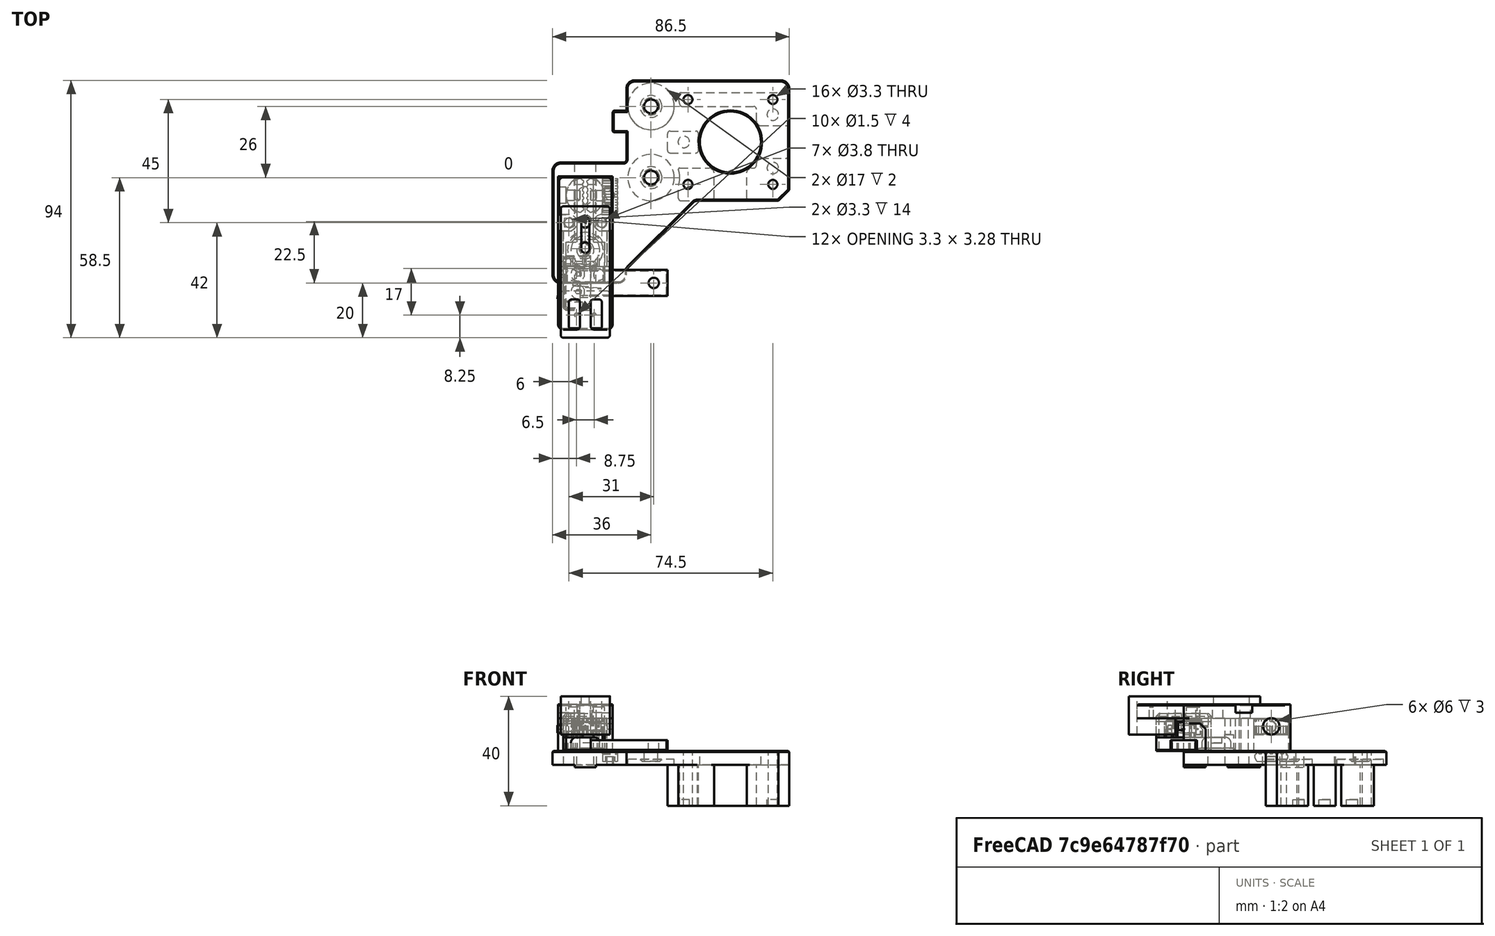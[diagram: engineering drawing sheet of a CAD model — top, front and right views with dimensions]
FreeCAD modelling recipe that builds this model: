
FCSTD DOCUMENT  (FreeCAD 0.19R24291 (Git))
Label: endstop
License: Other
LicenseURL: GPL3
objects: Part::Cylinder×31, Part::Box×27, Part::Cut×25, Part::Feature×20, Part::MultiFuse×18, Part::Chamfer×12, Part::Fillet×7, App::Part×3, Part::MultiCommon×1
note: 141 computed .brp shape members not serialized (recipe doc carries the construction recipe); baked Part::Feature solids carry a one-line shape summary decoded from their .brp

FEATURE [Part::Feature] Cut002008023012009006003002001  label="Cut002008023012009006003003"
  Placement = pos=(15,44,-35) rot=(0,0,1;0rad)
  shape: bbox 86.5 x 74 x 20 mm, 140 faces (baked)
FEATURE [Part::Feature] Fusion001001001001  label="switch"
  Placement = pos=(0,0,6) rot=(0,0,1;0rad)
  shape: bbox 13 x 12.18 x 6 mm, 43 faces (baked)
FEATURE [Part::Cylinder] Cylinder
  Angle = 360
  AttacherType = Attacher::AttachEngine3D
  Height = 1
  Placement = pos=(0,12,0) rot=(0,0,1;0rad)
  Radius = 6.5
FEATURE [Part::Cylinder] Cylinder001
  Angle = 360
  AttacherType = Attacher::AttachEngine3D
  Height = 4
  Placement = pos=(0,12,3) rot=(0,0,1;0rad)
  Radius = 2
FEATURE [Part::Cylinder] Cylinder002
  Angle = 360
  AttacherType = Attacher::AttachEngine3D
  Height = 4
  Placement = pos=(0,12,1) rot=(0,0,1;0rad)
  Radius = 5.25
FEATURE [Part::Fillet] Fillet
  Base = -> Cylinder002
  Edges = 1 edges r=2: [Edge1]
FEATURE [Part::Cut] Cut
  Base = -> Fillet
  Tool = -> Cylinder001
FEATURE [Part::Cylinder] Cylinder003
  Angle = 360
  AttacherType = Attacher::AttachEngine3D
  Height = 4
  Placement = pos=(-3.25,5.25,4) rot=(0,0,1;0rad)
  Radius = 0.75
FEATURE [Part::Cylinder] Cylinder004
  Angle = 360
  AttacherType = Attacher::AttachEngine3D
  Height = 4
  Placement = pos=(3.25,5.25,4) rot=(0,0,1;0rad)
  Radius = 0.75
FEATURE [Part::Box] Box  label="Cube"
  AttacherType = Attacher::AttachEngine3D
  Height = 5
  Length = 20
  Placement = pos=(-10,0,12) rot=(0,0,1;0rad)
  Width = 15
FEATURE [Part::Cylinder] Cylinder005
  Angle = 360
  AttacherType = Attacher::AttachEngine3D
  Height = 3
  Placement = pos=(6,22,0) rot=(0,0,1;0rad)
  Radius = 3
FEATURE [Part::Cylinder] Cylinder006
  Angle = 360
  AttacherType = Attacher::AttachEngine3D
  Height = 3
  Placement = pos=(-6,22,0) rot=(0,0,1;0rad)
  Radius = 3
FEATURE [Part::Box] Box001  label="Cube001"
  AttacherType = Attacher::AttachEngine3D
  Height = 17
  Length = 20
  Placement = pos=(-10,15,0) rot=(0,0,1;0rad)
  Width = 24
FEATURE [Part::Box] Box003  label="Cube003"
  AttacherType = Attacher::AttachEngine3D
  Height = 17
  Length = 3
  Placement = pos=(-10,0,0) rot=(0,0,1;0rad)
  Width = 39
FEATURE [Part::Cylinder] Cylinder007
  Angle = 360
  AttacherType = Attacher::AttachEngine3D
  Height = 6
  Placement = pos=(0,32,0) rot=(0,0,1;0rad)
  Radius = 7
FEATURE [Part::Cylinder] Cylinder008
  Angle = 360
  AttacherType = Attacher::AttachEngine3D
  Height = 6
  Placement = pos=(0,12,0) rot=(0,0,1;0rad)
  Radius = 7
FEATURE [Part::MultiFuse] Fusion
  Shapes = -> [Cylinder008,Cylinder007]
FEATURE [Part::Cylinder] Cylinder009
  Angle = 360
  AttacherType = Attacher::AttachEngine3D
  Height = 42
  Placement = pos=(6,22,0) rot=(0,0,1;0rad)
  Radius = 1.65
FEATURE [Part::Cylinder] Cylinder010
  Angle = 360
  AttacherType = Attacher::AttachEngine3D
  Height = 42
  Placement = pos=(-6,22,0) rot=(0,0,1;0rad)
  Radius = 1.65
FEATURE [Part::MultiFuse] Fusion001001001003
  Shapes = -> [Cylinder009,Cylinder010]
FEATURE [Part::MultiFuse] Fusion001001001004
  Placement = pos=(0,0,14) rot=(0,0,1;0rad)
  Shapes = -> [Cylinder006,Cylinder005]
FEATURE [Part::Box] Box004  label="Cube004"
  AttacherType = Attacher::AttachEngine3D
  Height = 10
  Length = 10
  Placement = pos=(6,19,14) rot=(0,0,1;0rad)
  Width = 6
FEATURE [Part::Box] Box005  label="Cube005"
  AttacherType = Attacher::AttachEngine3D
  Height = 10
  Length = 10
  Placement = pos=(-16,19,14) rot=(0,0,1;0rad)
  Width = 6
FEATURE [Part::MultiFuse] Fusion001001001005
  Shapes = -> [Box005,Box004]
FEATURE [Part::Box] Box006  label="Cube006"
  AttacherType = Attacher::AttachEngine3D
  Height = 12
  Length = 6
  Placement = pos=(-3,13,0) rot=(0,0,1;0rad)
  Width = 32
FEATURE [Part::MultiFuse] Fusion001001001006
  Placement = pos=(0,0,8) rot=(0,0,1;0rad)
  Shapes = -> [Cylinder004,Cylinder003]
FEATURE [Part::Box] Box007  label="Cube007"
  AttacherType = Attacher::AttachEngine3D
  Height = 17
  Length = 3
  Placement = pos=(7,0,0) rot=(0,0,1;0rad)
  Width = 39
FEATURE [Part::MultiFuse] Fusion001001001008
  Shapes = -> [Box007,Box001,Box,Box003]
FEATURE [Part::Cut] Cut002008023012009006003002002
  Base = -> Fusion001001001008
  Tool = -> Fusion
FEATURE [Part::Cut] Cut002008023012009006003002003
  Base = -> Cut002008023012009006003002002
  Tool = -> Box006
FEATURE [Part::Cut] Cut002008023012009006003002004
  Base = -> Cut002008023012009006003002003
  Tool = -> Fusion001001001003
FEATURE [Part::Cut] Cut002008023012009006003002005
  Base = -> Cut002008023012009006003002004
  Tool = -> Fusion001001001005
FEATURE [Part::Cut] Cut002008023012009006003002006  label="base-endstop-mount-template"
  Base = -> Cut002008023012009006003002005
  Tool = -> Fusion001001001004
FEATURE [Part::Feature] Cut002008023012009006003002006001  label="base-endstop-mount-template001"
  shape: bbox 20 x 39 x 17 mm, 32 faces (baked)
FEATURE [Part::Fillet] Fillet001
  Base = -> Cut002008023012009006003002006001
  Edges = 4 edges r=2: [Edge26,Edge28,Edge77,Edge104]
FEATURE [Part::Chamfer] Chamfer
  Base = -> Fillet001
  Edges = 2 edges r=2: [Edge93,Edge110]
FEATURE [Part::Chamfer] Chamfer001
  Base = -> Chamfer
  Edges = 10 edges r=0.4: [Edge30,Edge39,Edge70,Edge71,Edge74,Edge76,Edge77,Edge79,Edge82,Edge84]
FEATURE [Part::Feature] Cut002008023012009006003002006002002  label="base-endstop-mount-template002"
  shape: bbox 20 x 39 x 17 mm, 32 faces (baked)
FEATURE [Part::Box] Box008  label="Cube008"
  AttacherType = Attacher::AttachEngine3D
  Height = 12
  Length = 16
  Placement = pos=(-8,0,-2) rot=(0,0,1;0rad)
  Width = 19
FEATURE [Part::Fillet] Fillet002
  Base = -> Cut002008023012009006003002006002002
  Edges = 4 edges r=2: [Edge26,Edge28,Edge77,Edge104]
FEATURE [Part::Chamfer] Chamfer002
  Base = -> Fillet002
  Edges = 10 edges r=0.4: [Edge1,Edge9,Edge10,Edge13,Edge15,Edge16,Edge18,Edge20,Edge22,Edge24]
FEATURE [Part::Cylinder] Cylinder011
  Angle = 360
  AttacherType = Attacher::AttachEngine3D
  Height = 10
  Placement = pos=(5,3,6) rot=(0,0,1;0rad)
  Radius = 2
FEATURE [Part::Cylinder] Cylinder012
  Angle = 360
  AttacherType = Attacher::AttachEngine3D
  Height = 10
  Placement = pos=(-5,3,6) rot=(0,0,1;0rad)
  Radius = 2
FEATURE [Part::MultiFuse] Fusion001001001009
  Shapes = -> [Cylinder012,Cylinder011]
FEATURE [Part::Box] Box009  label="Cube009"
  AttacherType = Attacher::AttachEngine3D
  Height = 12
  Length = 22
  Placement = pos=(-11,-12,-2) rot=(0,0,1;0rad)
  Width = 19
FEATURE [Part::Box] Box010  label="Cube010"
  AttacherType = Attacher::AttachEngine3D
  Height = 3
  Length = 16
  Placement = pos=(-8,0,10) rot=(0,0,1;0rad)
  Width = 6
FEATURE [Part::Cut] Cut002008023012009006003002006002003
  Base = -> Chamfer002
  Tool = -> Box008
FEATURE [Part::Box] Box011  label="Cube011"
  AttacherType = Attacher::AttachEngine3D
  Height = 3
  Length = 16
  Placement = pos=(-8,0,9) rot=(0,0,1;0rad)
  Width = 19
FEATURE [Part::Cut] Cut002008023012009006003002006002004
  Base = -> Cut002008023012009006003002006002003
  Tool = -> Box011
FEATURE [Part::MultiFuse] Fusion001001001010
  Shapes = -> [Cut002008023012009006003002006002004,Box010]
FEATURE [Part::Cut] Cut002008023012009006003002006002005
  Base = -> Fusion001001001010
  Tool = -> Fusion001001001009
FEATURE [Part::Chamfer] Chamfer003
  Base = -> Cut002008023012009006003002006002005
  Edges = 2 edges r=2: [Edge106,Edge148]
FEATURE [Part::Chamfer] Chamfer004
  Base = -> Box009
  Edges = 1 edges r=2: [Edge12]
  Placement = pos=(0,1,0) rot=(0,0,1;0rad)
FEATURE [Part::Cut] Cut002008023012009006003002006002006  label="HTU2X-sensor-mounter"
  Base = -> Chamfer003
  Tool = -> Chamfer004
FEATURE [Part::Cut] Cut002008023012009006003002006002006002
  Base = -> Chamfer001
  Tool = -> Fusion001001001006
FEATURE [Part::Cylinder] Cylinder013
  Angle = 360
  AttacherType = Attacher::AttachEngine3D
  Height = 5.5
  Placement = pos=(0,32,6.25) rot=(0,0,1;0rad)
  Radius = 6.5
FEATURE [Part::Box] Box012  label="Cube012"
  AttacherType = Attacher::AttachEngine3D
  Height = 10
  Length = 10
  Placement = pos=(-9,20.75,2.25) rot=(0,0,1;0rad)
  Width = 19
FEATURE [Part::Cylinder] Cylinder014
  Angle = 360
  AttacherType = Attacher::AttachEngine3D
  Height = 12
  Placement = pos=(0,32,0) rot=(0,0,1;0rad)
  Radius = 7
FEATURE [Part::Box] Box013  label="Cube013"
  AttacherType = Attacher::AttachEngine3D
  Height = 16
  Length = 10
  Placement = pos=(4,20.75,-2.25) rot=(0,0,1;0rad)
  Width = 19
FEATURE [Part::Box] Box014  label="Cube014"
  AttacherType = Attacher::AttachEngine3D
  Height = 16
  Length = 10
  Placement = pos=(-10,20.75,-2.25) rot=(0,0,1;0rad)
  Width = 19
FEATURE [Part::Cut] Cut002008023012009006003002006002006002003
  Base = -> Cylinder014
  Tool = -> Box014
FEATURE [Part::Cut] Cut002008023012009006003002006002006002004
  Base = -> Cut002008023012009006003002006002006002003
  Tool = -> Box013
FEATURE [Part::Feature] Cut002008023012009006003002006002006002004001  label="Cut002008023012009006003002006002006002005"
  shape: bbox 4 x 14 x 12 mm, 6 faces (baked)
FEATURE [Part::Cut] Cut002008023012009006003002006002006002004002
  Base = -> Cut002008023012009006003002006002006002
  Tool = -> Cut002008023012009006003002006002006002004001
FEATURE [Part::Cut] Cut002008023012009006003002006002006002004003
  Base = -> Cut002008023012009006003002006002006
  Tool = -> Cut002008023012009006003002006002006002004
FEATURE [Part::Cylinder] Cylinder015
  Angle = 360
  AttacherType = Attacher::AttachEngine3D
  Height = 3
  Placement = pos=(7,32,9) rot=(0,1,0;1.5708rad)
  Radius = 3
FEATURE [Part::Cylinder] Cylinder016
  Angle = 360
  AttacherType = Attacher::AttachEngine3D
  Height = 16
  Placement = pos=(-2e-15,32,9) rot=(0,1,0;1.5708rad)
  Radius = 1.9
FEATURE [Part::MultiFuse] Fusion001001001011
  Shapes = -> [Cylinder016,Cylinder015]
FEATURE [Part::Feature] Fusion001001001011001  label="Fusion001001001012"
  shape: bbox 16 x 6 x 6 mm, 7 faces (baked)
FEATURE [Part::Cut] Cut002008023012009006003002006002006002004004  label="endstop-mount"
  Base = -> Cut002008023012009006003002006002006002004002
  Tool = -> Fusion001001001011001
FEATURE [Part::Cut] Cut002008023012009006003002006002006002004005  label="sensor-mount"
  Base = -> Cut002008023012009006003002006002006002004003
  Tool = -> Fusion001001001011
FEATURE [Part::Box] Box015  label="Cube015"
  AttacherType = Attacher::AttachEngine3D
  Height = 10
  Length = 10
  Placement = pos=(3.75,20.75,2.25) rot=(0,0,1;0rad)
  Width = 19
FEATURE [Part::Cut] Cut002008023012009006003002006002006002004006
  Base = -> Cylinder013
  Tool = -> Box015
FEATURE [Part::Cut] Cut002008023012009006003002006002006002004007
  Base = -> Cut002008023012009006003002006002006002004006
  Tool = -> Box012
FEATURE [Part::Fillet] Fillet003
  Base = -> Cut002008023012009006003002006002006002004007
  Edges = 2 edges r=1: [Edge2,Edge8]
FEATURE [Part::Cylinder] Cylinder017
  Angle = 360
  AttacherType = Attacher::AttachEngine3D
  Height = 10
  Placement = pos=(2,32,9) rot=(0,1,0;1.5708rad)
  Radius = 1.7
FEATURE [Part::Cut] Cut002008023012009006003002006002006002004008
  Base = -> Fillet003
  Tool = -> Cylinder017
FEATURE [Part::Cylinder] Cylinder018
  Angle = 360
  AttacherType = Attacher::AttachEngine3D
  Height = 5.5
  Placement = pos=(1,27,6.25) rot=(0,0,1;0rad)
  Radius = 0.5
FEATURE [Part::Cylinder] Cylinder020
  Angle = 360
  AttacherType = Attacher::AttachEngine3D
  Height = 5.5
  Placement = pos=(1,35,6.25) rot=(0,0,1;0rad)
  Radius = 0.5
FEATURE [Part::Cylinder] Cylinder021
  Angle = 360
  AttacherType = Attacher::AttachEngine3D
  Height = 5.5
  Placement = pos=(1,37,6.25) rot=(0,0,1;0rad)
  Radius = 0.5
FEATURE [Part::Cylinder] Cylinder022
  Angle = 360
  AttacherType = Attacher::AttachEngine3D
  Height = 5.5
  Placement = pos=(1,31,6.25) rot=(0,0,1;0rad)
  Radius = 0.5
FEATURE [Part::Cylinder] Cylinder023
  Angle = 360
  AttacherType = Attacher::AttachEngine3D
  Height = 5.5
  Placement = pos=(1,29,6.25) rot=(0,0,1;0rad)
  Radius = 0.5
FEATURE [Part::Cylinder] Cylinder024
  Angle = 360
  AttacherType = Attacher::AttachEngine3D
  Height = 5.5
  Placement = pos=(1,33,6.25) rot=(0,0,1;0rad)
  Radius = 0.5
FEATURE [Part::MultiFuse] Fusion001001001011002  label="wire-clamp"
  Shapes = -> [Cylinder024,Cylinder022,Cylinder020,Cylinder021,Cylinder023,Cylinder018,Cut002008023012009006003002006002006002004008]
FEATURE [Part::Feature] Cut002008023012009006003002006002006002004004001  label="endstop-mount001"
  shape: bbox 20 x 39 x 17 mm, 57 faces (baked)
FEATURE [Part::Feature] Fusion001001001011002001  label="wire-clamp001"
  shape: bbox 3.25 x 12.25 x 5.5 mm, 20 faces (baked)
FEATURE [Part::Feature] Part__Mirroring001001  label="wire-clamp002 (Mirror #2)001"
  shape: bbox 3.25 x 12.25 x 5.5 mm, 20 faces (baked)
FEATURE [Part::Feature] Part__Mirroring001002  label="sensor-mount001 (Mirror #1)001"
  shape: bbox 20 x 39 x 17 mm, 59 faces (baked)
FEATURE [App::Part] Part001  label="HTU2X-mounter"
  Group = -> [Part__Mirroring001001,Part__Mirroring001002]
  Origin = -> Origin001
FEATURE [Part::Feature] Fusion001001001011002002  label="switch001"
  Placement = pos=(0,0,6) rot=(0,0,1;0rad)
  shape: bbox 13 x 12.18 x 6 mm, 43 faces (baked)
FEATURE [App::Part] Part  label="Y-endstop"
  Group = -> [Cut002008023012009006003002006002006002004004001,Fusion001001001011002001,Fusion001001001011002002]
  Origin = -> Origin
FEATURE [Part::Box] Box018  label="Cube018"
  AttacherType = Attacher::AttachEngine3D
  Height = 4
  Length = 30
  Placement = pos=(0,-4.8,0) rot=(0,0,1;0rad)
  Width = 9.6
FEATURE [Part::Feature] Fusion001001001011002003  label="switch002"
  Placement = pos=(-8,2e-15,5) rot=(0,0,-1;1.5708rad)
  shape: bbox 12.18 x 13 x 6 mm, 43 faces (baked)
FEATURE [Part::Box] Box019  label="Cube019"
  AttacherType = Attacher::AttachEngine3D
  Height = 5
  Length = 10
  Placement = pos=(-8,-10,0) rot=(0,0,1;0rad)
  Width = 20
FEATURE [Part::Box] Box020  label="Cube020"
  AttacherType = Attacher::AttachEngine3D
  Height = 7
  Length = 7
  Placement = pos=(-8,-10,5) rot=(0,0,1;0rad)
  Width = 3
FEATURE [Part::Box] Box021  label="Cube021"
  AttacherType = Attacher::AttachEngine3D
  Height = 7
  Length = 7
  Placement = pos=(-8,7,5) rot=(0,0,1;0rad)
  Width = 3
FEATURE [Part::Box] Box022  label="Cube022"
  AttacherType = Attacher::AttachEngine3D
  Height = 3
  Length = 10
  Placement = pos=(-8,-10,10.5) rot=(0,0,1;0rad)
  Width = 20
FEATURE [Part::Chamfer] Chamfer009
  Base = -> Box019
  Edges = 2 edges r=1: [Edge1,Edge3]
FEATURE [Part::Chamfer] Chamfer010
  Base = -> Box021
  Edges = 1 edges r=1: [Edge3]
FEATURE [Part::Chamfer] Chamfer011
  Base = -> Box020
  Edges = 1 edges r=1: [Edge1]
FEATURE [Part::Chamfer] Chamfer012
  Base = -> Box022
  Edges = 2 edges r=1: [Edge1,Edge3]
FEATURE [Part::Chamfer] Chamfer013
  Base = -> Chamfer012
  Edges = 5 edges r=1: [Edge1,Edge5,Edge6,Edge7,Edge8]
FEATURE [Part::Cylinder] Cylinder025
  Angle = 360
  AttacherType = Attacher::AttachEngine3D
  Height = 5
  Placement = pos=(25,0,0) rot=(0,0,1;0rad)
  Radius = 1.9
FEATURE [Part::Cut] Cut002008023012009006003002006002006002004004002
  Base = -> Box018
  Tool = -> Cylinder025
FEATURE [Part::MultiFuse] Fusion001001001011002004
  Shapes = -> [Chamfer009,Cut002008023012009006003002006002006002004004002]
FEATURE [Part::Cylinder] Cylinder026
  Angle = 360
  AttacherType = Attacher::AttachEngine3D
  Height = 5
  Placement = pos=(-2.75,3.25,0) rot=(0,0,1;0rad)
  Radius = 2.5
FEATURE [Part::Cylinder] Cylinder027
  Angle = 360
  AttacherType = Attacher::AttachEngine3D
  Height = 5
  Placement = pos=(-2.75,-3.25,0) rot=(0,0,1;0rad)
  Radius = 2.5
FEATURE [Part::Cylinder] Cylinder028
  Angle = 360
  AttacherType = Attacher::AttachEngine3D
  Height = 18
  Placement = pos=(-2.75,-3.25,0) rot=(0,0,1;0rad)
  Radius = 0.85
FEATURE [Part::Cylinder] Cylinder029
  Angle = 360
  AttacherType = Attacher::AttachEngine3D
  Height = 18
  Placement = pos=(-2.75,3.25,0) rot=(0,0,1;0rad)
  Radius = 0.85
FEATURE [Part::MultiFuse] Fusion001001001011002005
  Shapes = -> [Cylinder028,Cylinder029]
FEATURE [Part::Cut] Cut002008023012009006003002006002006002004004003
  Base = -> Chamfer013
  Placement = pos=(0,0,0.5) rot=(0,0,1;0rad)
  Tool = -> Fusion001001001011002005
FEATURE [Part::MultiFuse] Fusion001001001011002006
  Placement = pos=(0,0,12) rot=(0,0,1;0rad)
  Shapes = -> [Cylinder027,Cylinder026]
FEATURE [Part::Feature] Fusion001001001011002004001  label="Fusion001001001011002007"
  shape: bbox 38 x 20 x 5 mm, 13 faces (baked)
FEATURE [Part::Chamfer] Chamfer014
  Base = -> Fusion001001001011002004001
  Edges = 12 edges r=0.4: [Edge4,Edge10,Edge12,Edge14,Edge16,Edge18,Edge22,Edge23,Edge24,Edge29,Edge30,Edge31]
FEATURE [Part::Cut] Cut002008023012009006003002006002006002004004004
  Base = -> Cut002008023012009006003002006002006002004004003
  Placement = pos=(0,0,-0.25) rot=(0,0,1;0rad)
  Tool = -> Fusion001001001011002006
FEATURE [Part::MultiFuse] Fusion001001001011002004002
  Shapes = -> [Cut002008023012009006003002006002006002004004004,Chamfer010,Chamfer011]
FEATURE [Part::Feature] Fusion001001001011002004002001  label="Fusion001001001011002004003"
  shape: bbox 10 x 20 x 8.75 mm, 25 faces (baked)
FEATURE [Part::Feature] Cut002008023012009006003002006002006002004004005001
  shape: bbox 38 x 20 x 5 mm, 29 faces (baked)
FEATURE [App::Part] Part002  label="X-endstop"
  Group = -> [Fusion001001001011002004002001,Fusion001001001011002003,Cut002008023012009006003002006002006002004004005001]
  Origin = -> Origin002
FEATURE [Part::Feature] Fusion001001001011002004002002  label="switch003"
  Placement = pos=(0,0,6) rot=(0,0,1;0rad)
  shape: bbox 13 x 12.18 x 6 mm, 43 faces (baked)
FEATURE [Part::Feature] Fusion001001001011002004002003  label="wire-clamp002"
  Placement = pos=(0,0,0) rot=(0,1,0;1.5708rad)
  shape: bbox 5.5 x 12.25 x 3.25 mm, 20 faces (baked)
FEATURE [Part::Feature] Cut002008023012009006003002006002006002004004005002  label="endstop-mount002"
  shape: bbox 20 x 39 x 17 mm, 57 faces (baked)
FEATURE [Part::Box] Box023  label="Cube023"
  AttacherType = Attacher::AttachEngine3D
  Height = 3
  Length = 18
  Placement = pos=(-9,-4,17) rot=(0,0,1;0rad)
  Width = 32
FEATURE [Part::Box] Box024  label="Cube024"
  AttacherType = Attacher::AttachEngine3D
  Height = 14
  Length = 18
  Placement = pos=(-9,-20,6) rot=(0,0,1;0rad)
  Width = 17
FEATURE [Part::Box] Box025  label="Cube025"
  AttacherType = Attacher::AttachEngine3D
  Height = 5
  Length = 3
  Placement = pos=(-1.5,12.5,17) rot=(0,0,1;0rad)
  Width = 10
FEATURE [Part::Cylinder] Cylinder032
  Angle = 360
  AttacherType = Attacher::AttachEngine3D
  Height = 10
  Placement = pos=(0,12.5,12.5) rot=(0,0,1;0rad)
  Radius = 1.5
FEATURE [Part::Cylinder] Cylinder033
  Angle = 360
  AttacherType = Attacher::AttachEngine3D
  Height = 10
  Placement = pos=(0,22.5,12.5) rot=(0,0,1;0rad)
  Radius = 1.5
FEATURE [Part::MultiFuse] Fusion001001001011002004002005
  Shapes = -> [Box025,Cylinder032,Cylinder033]
FEATURE [Part::Box] Box026  label="Cube026"
  AttacherType = Attacher::AttachEngine3D
  Height = 16
  Length = 4
  Placement = pos=(-6,-17,6) rot=(0,0,1;0rad)
  Width = 11
FEATURE [Part::Box] Box027  label="Cube027"
  AttacherType = Attacher::AttachEngine3D
  Height = 16
  Length = 4
  Placement = pos=(2,-17,6) rot=(0,0,1;0rad)
  Width = 11
FEATURE [Part::MultiFuse] Fusion001001001011002004002008
  Shapes = -> [Box027,Box026]
FEATURE [Part::Fillet] Fillet004
  Base = -> Fusion001001001011002004002008
  Edges = 8 edges r=1: [Edge1,Edge3,Edge5,Edge7,Edge13,Edge15,Edge17,Edge19]
FEATURE [Part::Fillet] Fillet005
  Base = -> Box024
  Edges = 4 edges r=1: [Edge1,Edge3,Edge5,Edge7]
FEATURE [Part::Cut] Cut002008023012009006003002006002006002004004005004
  Base = -> Fillet005
  Tool = -> Fillet004
FEATURE [Part::Cut] Cut002008023012009006003002006002006002004004005005
  Base = -> Box023
  Tool = -> Fusion001001001011002004002005
FEATURE [Part::Fillet] Fillet006
  Base = -> Cut002008023012009006003002006002006002004004005005
  Edges = 2 edges r=1: [Edge3,Edge15]
FEATURE [Part::MultiFuse] Fusion001001001011002004002009
  Shapes = -> [Fillet006,Cut002008023012009006003002006002006002004004005004]
FEATURE [Part::Feature] Chamfer015001
  shape: bbox 20 x 39 x 17 mm, 61 faces (baked)
FEATURE [Part::Box] Box028  label="Cube028"
  AttacherType = Attacher::AttachEngine3D
  Height = 10
  Length = 20
  Placement = pos=(-10,0,12) rot=(0,0,1;0rad)
  Width = 17
FEATURE [Part::Feature] Cut002008023012009006003002006002006002004004005006  label="endstop-mount003"
  shape: bbox 20 x 39 x 17 mm, 57 faces (baked)
FEATURE [Part::Box] Box029  label="Cube029"
  AttacherType = Attacher::AttachEngine3D
  Height = 5
  Length = 20
  Placement = pos=(-10,-0.5,12) rot=(0,0,1;0rad)
  Width = 3
FEATURE [Part::MultiCommon] Common
  Placement = pos=(0,-17,0) rot=(0,0,1;0rad)
  Shapes = -> [Cut002008023012009006003002006002006002004004005002,Box028]
FEATURE [Part::Chamfer] Chamfer015002
  Base = -> Box029
  Edges = 2 edges r=0.4: [Edge2,Edge6]
FEATURE [Part::MultiFuse] Fusion001001001011002004002010  label="y-endstop-17mm-extend"
  Shapes = -> [Cut002008023012009006003002006002006002004004005006,Chamfer015002,Common]
